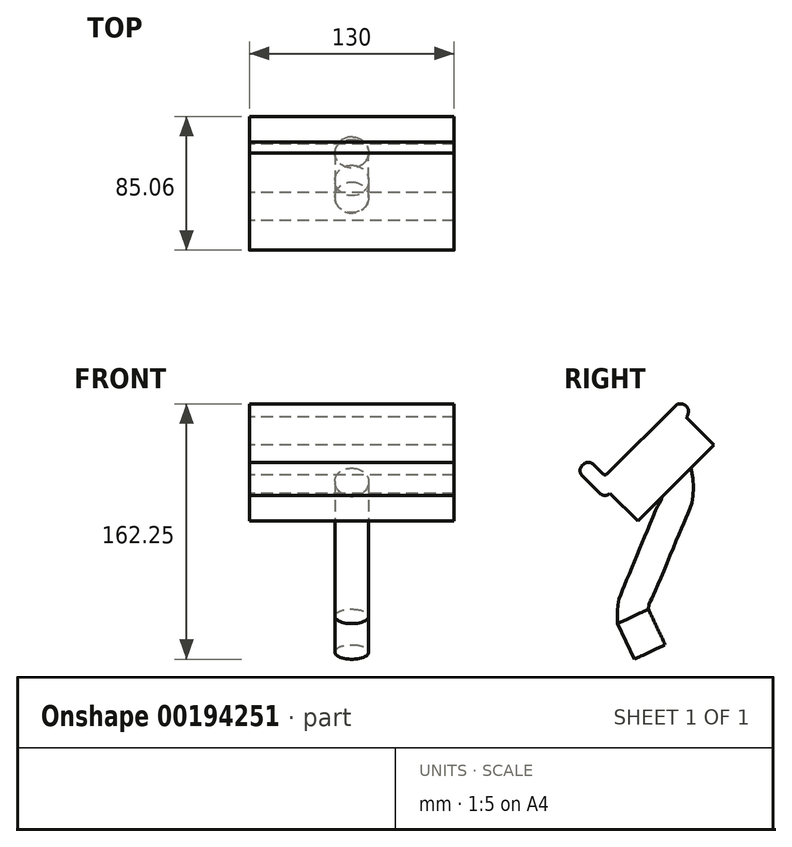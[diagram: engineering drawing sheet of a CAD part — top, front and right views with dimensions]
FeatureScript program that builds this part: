
annotation { "Feature Type Name" : "Feature", "Feature Type Description" : "" }
export const myFeature = defineFeature(function(context is Context, id is Id, definition is map)
    precondition{}
    {
        {
            var Q0;
            Q0=qCreatedBy(makeId("Right.planeOp"),FACE);
            var sketch = newSketch(context, id + "F0", { "sketchPlane" : qUnion([Q0])});
            skLineSegment(sketch, "E0", {"start": v(1.41, 90.56) * mm, "end": v(45.96, 135.1) * mm});
            skLineSegment(sketch, "E1", {"start": v(45.96, 135.1) * mm, "end": v(48.03, 135.1) * mm});
            skLineSegment(sketch, "E2", {"start": v(51.57, 126.57) * mm, "end": v(3.18, 78.18) * mm});
            skLineSegment(sketch, "E3", {"start": v(-3.18, 78.18) * mm, "end": v(-14.5, 89.5) * mm});
            skLineSegment(sketch, "E4", {"start": v(-1.41, 90.56) * mm, "end": v(-7.42, 96.57) * mm});
            skLineSegment(sketch, "E5", {"start": v(-14.5, 95.86) * mm, "end": v(-13.79, 96.57) * mm});
            skLineSegment(sketch, "E6", {"start": v(0, 75) * mm, "end": v(0, 0) * mm, "construction": true});
            skPoint(sketch, "E7.visualSharp", {"position": v(60.1, 135.1) * mm});
            skArc(sketch, "E7.filletArc", {"start": v(51.57, 126.57) * mm, "mid": v(52.65, 132.02) * mm, "end": v(48.03, 135.1) * mm});
            skPoint(sketch, "E8.visualSharp", {"position": v(-17.68, 92.68) * mm});
            skArc(sketch, "E8.filletArc", {"start": v(-14.5, 95.86) * mm, "mid": v(-15.81, 92.68) * mm, "end": v(-14.5, 89.5) * mm});
            skPoint(sketch, "E9.visualSharp", {"position": v(-10.6, 99.75) * mm});
            skArc(sketch, "E9.filletArc", {"start": v(-7.42, 96.57) * mm, "mid": v(-10.6, 97.88) * mm, "end": v(-13.79, 96.57) * mm});
            skPoint(sketch, "E10.visualSharp", {"position": v(0, 75) * mm});
            skArc(sketch, "E10.filletArc", {"start": v(-3.18, 78.18) * mm, "mid": v(0, 76.86) * mm, "end": v(3.18, 78.18) * mm});
            skPoint(sketch, "E11.visualSharp", {"position": v(0, 89.14) * mm});
            skArc(sketch, "E11.filletArc", {"start": v(-1.41, 90.56) * mm, "mid": v(0, 89.97) * mm, "end": v(1.41, 90.56) * mm});
            skSolve(sketch);
        }
        {
            var Q0;
            Q0=makeQuery(id+"F0.imprint","IMPRINT",FACE,{"disambiguationData":[TD([[makeQuery(id+"F0.imprint","IMPRINT",EDGE,{"derivedFrom":sQuery(id+"F0.wireOp",EDGE,"E0")}),-1.0]])]});
            extrude(context, id + "F1", {"entities" : qUnion([Q0]), "endBound" : BoundingType.SYMMETRIC, "depth" : 130 * mm});
        }
        {
            var Q0;
            Q0=qCreatedBy(makeId("Right.planeOp"),FACE);
            var sketch = newSketch(context, id + "F2", { "sketchPlane" : qUnion([Q0])});
            skLineSegment(sketch, "E12.0", {"start": v(51.57, 126.57) * mm, "end": v(3.18, 78.18) * mm});
            skFitSpline(sketch, "E13", {"points": [v(38.31, 113.31) * mm, v(42.8, 67.4) * mm, v(34.51, 47.82) * mm, v(21.12, 15.65) * mm, v(17.7, 0) * mm], "startDerivative": vector(105.9, -286.99) * mm, "endDerivative": vector(1.09, -114.05) * mm});
            skSolve(sketch);
        }
        {
            var Q0;
            Q0=makeQuery(id+"F1.opExtrude","SWEPT_FACE",FACE,{"disambiguationData":[OSD([sQuery(id+"F0.wireOp",EDGE,"E2")])]});
            var sketch = newSketch(context, id + "F3", { "sketchPlane" : qUnion([Q0])});
            skCircle(sketch, "E14", {"center": v(0, 107.34) * mm, "radius": 10.77 * mm});
            skSolve(sketch);
        }
        {
            var Q0;
            Q0=makeQuery(id+"F3.imprint","IMPRINT",FACE,{"disambiguationData":[TD([[makeQuery(id+"F3.imprint","IMPRINT",EDGE,{"derivedFrom":sQuery(id+"F3.wireOp",EDGE,"E14")}),1.0]])]});
            var Q1;
            Q1=sQuery(id+"F2.wireOp",EDGE,"E13");
            sweep(context, id + "F4", {"operationType" : NewBodyOperationType.ADD, "profiles" : qUnion([Q0]), "path" : qUnion([Q1])});
        }
        {
            var Q0;
            Q0=makeQuery(id+"F4.opSweep","CAP_FACE",FACE,{"disambiguationData":[OSD([sQuery(id+"F2.wireOp",VERTEX,"E13.end"),sQuery(id+"F3.wireOp",EDGE,"E14")])],"isStart":false});
            extrude(context, id + "F5", {"entities" : qUnion([Q0]), "operationType" : NewBodyOperationType.ADD, "depth" : 25 * mm});
        }
        {
            var Q0;
            Q0=makeQuery(id+"F1.opExtrude","SWEPT_FACE",FACE,{"disambiguationData":[OSD([sQuery(id+"F0.wireOp",EDGE,"E2")])]});
            var Q1;
            Q1=makeQuery(id+"F3.imprint","IMPRINT",FACE,{"disambiguationData":[TD([[makeQuery(id+"F3.imprint","IMPRINT",EDGE,{"derivedFrom":sQuery(id+"F3.wireOp",EDGE,"E14")}),1.0]])]});
            extrude(context, id + "F6", {"entities" : qUnion([Q0, Q1]), "operationType" : NewBodyOperationType.ADD, "depth" : 25 * mm});
        }
    });
